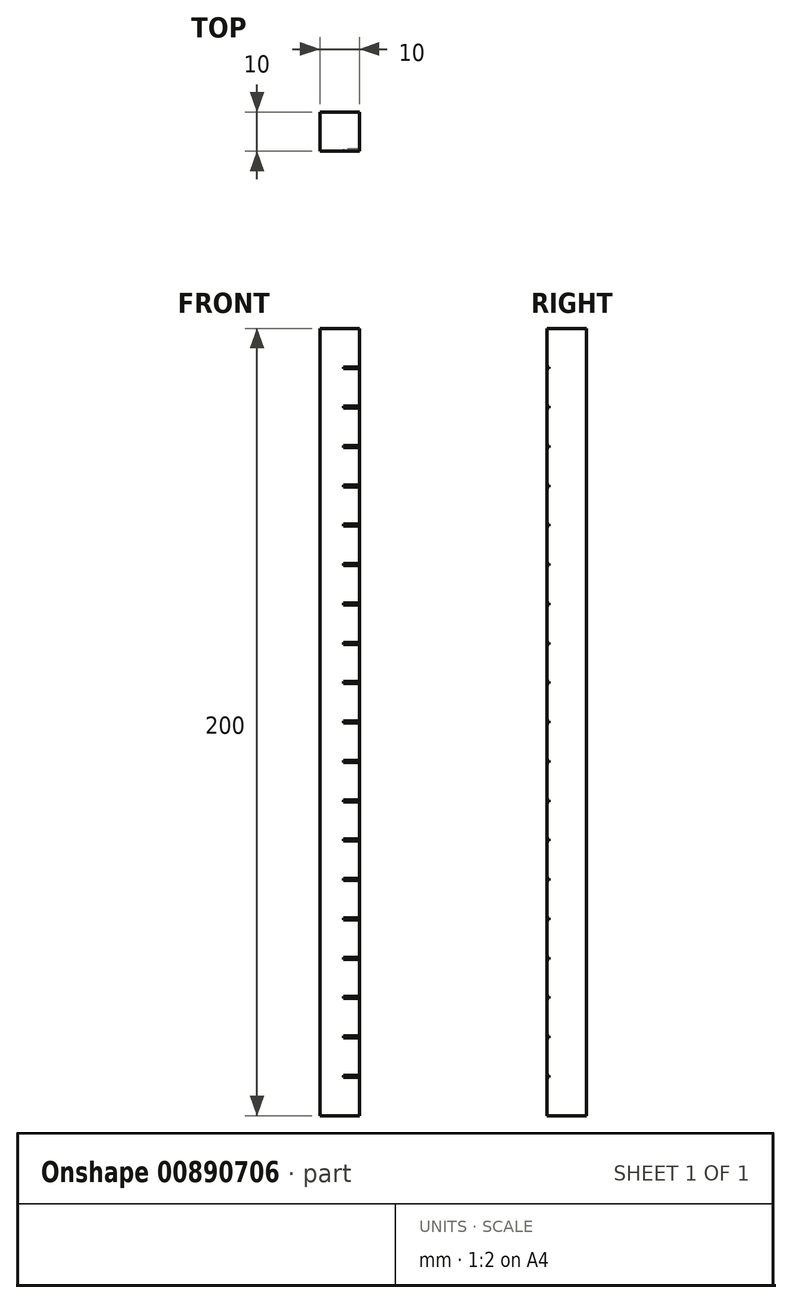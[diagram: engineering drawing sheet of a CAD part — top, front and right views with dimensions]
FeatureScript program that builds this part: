
annotation { "Feature Type Name" : "Feature", "Feature Type Description" : "" }
export const myFeature = defineFeature(function(context is Context, id is Id, definition is map)
    precondition{}
    {
        {
            var Q0;
            Q0=qCreatedBy(makeId("Top.planeOp"),FACE);
            var sketch = newSketch(context, id + "F0", { "sketchPlane" : qUnion([Q0])});
            skLineSegment(sketch, "E0.bottom", {"start": v(0, 0) * mm, "end": v(10, 0) * mm});
            skLineSegment(sketch, "E0.top", {"start": v(0, 10) * mm, "end": v(10, 10) * mm});
            skLineSegment(sketch, "E0.left", {"start": v(0, 0) * mm, "end": v(0, 10) * mm});
            skLineSegment(sketch, "E0.right", {"start": v(10, 0) * mm, "end": v(10, 10) * mm});
            skSolve(sketch);
        }
        {
            var Q0;
            Q0 = qSketchRegion(id + "F0", true);
            extrude(context, id + "F1", {"entities" : qUnion([Q0]), "depth" : 200 * mm, "offsetDistance" : 25 * mm});
        }
        {
            var Q0;
            Q0=makeQuery(id+"F1.opExtrude","SWEPT_FACE",FACE,{"disambiguationData":[OSD([sQuery(id+"F0.wireOp",EDGE,"E0.bottom")])]});
            var sketch = newSketch(context, id + "F2", { "sketchPlane" : qUnion([Q0])});
            skLineSegment(sketch, "E1", {"start": v(10, 0) * mm, "end": v(10, 10) * mm});
            skLineSegment(sketch, "E2.bottom", {"start": v(10, 9.75) * mm, "end": v(6, 9.75) * mm});
            skLineSegment(sketch, "E2.top", {"start": v(10, 10.25) * mm, "end": v(6, 10.25) * mm});
            skLineSegment(sketch, "E2.left", {"start": v(10, 9.75) * mm, "end": v(10, 10.25) * mm});
            skLineSegment(sketch, "E2.right", {"start": v(6, 9.75) * mm, "end": v(6, 10.25) * mm});
            skLineSegment(sketch, "E3.0.1.0", {"start": v(10, 20.25) * mm, "end": v(6, 20.25) * mm});
            skLineSegment(sketch, "E3.0.1.1", {"start": v(10, 19.75) * mm, "end": v(6, 19.75) * mm});
            skLineSegment(sketch, "E3.0.1.2", {"start": v(6, 19.75) * mm, "end": v(6, 20.25) * mm});
            skLineSegment(sketch, "E3.0.2.0", {"start": v(10, 30.25) * mm, "end": v(6, 30.25) * mm});
            skLineSegment(sketch, "E3.0.2.1", {"start": v(10, 29.75) * mm, "end": v(6, 29.75) * mm});
            skLineSegment(sketch, "E3.0.2.2", {"start": v(6, 29.75) * mm, "end": v(6, 30.25) * mm});
            skLineSegment(sketch, "E3.0.3.0", {"start": v(10, 40.25) * mm, "end": v(6, 40.25) * mm});
            skLineSegment(sketch, "E3.0.3.1", {"start": v(10, 39.75) * mm, "end": v(6, 39.75) * mm});
            skLineSegment(sketch, "E3.0.3.2", {"start": v(6, 39.75) * mm, "end": v(6, 40.25) * mm});
            skLineSegment(sketch, "E3.0.4.0", {"start": v(10, 50.25) * mm, "end": v(6, 50.25) * mm});
            skLineSegment(sketch, "E3.0.4.1", {"start": v(10, 49.75) * mm, "end": v(6, 49.75) * mm});
            skLineSegment(sketch, "E3.0.4.2", {"start": v(6, 49.75) * mm, "end": v(6, 50.25) * mm});
            skLineSegment(sketch, "E3.0.5.0", {"start": v(10, 60.25) * mm, "end": v(6, 60.25) * mm});
            skLineSegment(sketch, "E3.0.5.1", {"start": v(10, 59.75) * mm, "end": v(6, 59.75) * mm});
            skLineSegment(sketch, "E3.0.5.2", {"start": v(6, 59.75) * mm, "end": v(6, 60.25) * mm});
            skLineSegment(sketch, "E3.0.6.0", {"start": v(10, 70.25) * mm, "end": v(6, 70.25) * mm});
            skLineSegment(sketch, "E3.0.6.1", {"start": v(10, 69.75) * mm, "end": v(6, 69.75) * mm});
            skLineSegment(sketch, "E3.0.6.2", {"start": v(6, 69.75) * mm, "end": v(6, 70.25) * mm});
            skLineSegment(sketch, "E3.0.7.0", {"start": v(10, 80.25) * mm, "end": v(6, 80.25) * mm});
            skLineSegment(sketch, "E3.0.7.1", {"start": v(10, 79.75) * mm, "end": v(6, 79.75) * mm});
            skLineSegment(sketch, "E3.0.7.2", {"start": v(6, 79.75) * mm, "end": v(6, 80.25) * mm});
            skLineSegment(sketch, "E3.0.8.0", {"start": v(10, 90.25) * mm, "end": v(6, 90.25) * mm});
            skLineSegment(sketch, "E3.0.8.1", {"start": v(10, 89.75) * mm, "end": v(6, 89.75) * mm});
            skLineSegment(sketch, "E3.0.8.2", {"start": v(6, 89.75) * mm, "end": v(6, 90.25) * mm});
            skLineSegment(sketch, "E3.0.9.0", {"start": v(10, 100.25) * mm, "end": v(6, 100.25) * mm});
            skLineSegment(sketch, "E3.0.9.1", {"start": v(10, 99.75) * mm, "end": v(6, 99.75) * mm});
            skLineSegment(sketch, "E3.0.9.2", {"start": v(6, 99.75) * mm, "end": v(6, 100.25) * mm});
            skLineSegment(sketch, "E3.0.10.0", {"start": v(10, 110.25) * mm, "end": v(6, 110.25) * mm});
            skLineSegment(sketch, "E3.0.10.1", {"start": v(10, 109.75) * mm, "end": v(6, 109.75) * mm});
            skLineSegment(sketch, "E3.0.10.2", {"start": v(6, 109.75) * mm, "end": v(6, 110.25) * mm});
            skLineSegment(sketch, "E3.0.11.0", {"start": v(10, 120.25) * mm, "end": v(6, 120.25) * mm});
            skLineSegment(sketch, "E3.0.11.1", {"start": v(10, 119.75) * mm, "end": v(6, 119.75) * mm});
            skLineSegment(sketch, "E3.0.11.2", {"start": v(6, 119.75) * mm, "end": v(6, 120.25) * mm});
            skLineSegment(sketch, "E3.0.12.0", {"start": v(10, 130.25) * mm, "end": v(6, 130.25) * mm});
            skLineSegment(sketch, "E3.0.12.1", {"start": v(10, 129.75) * mm, "end": v(6, 129.75) * mm});
            skLineSegment(sketch, "E3.0.12.2", {"start": v(6, 129.75) * mm, "end": v(6, 130.25) * mm});
            skLineSegment(sketch, "E3.0.13.0", {"start": v(10, 140.25) * mm, "end": v(6, 140.25) * mm});
            skLineSegment(sketch, "E3.0.13.1", {"start": v(10, 139.75) * mm, "end": v(6, 139.75) * mm});
            skLineSegment(sketch, "E3.0.13.2", {"start": v(6, 139.75) * mm, "end": v(6, 140.25) * mm});
            skLineSegment(sketch, "E3.0.14.0", {"start": v(10, 150.25) * mm, "end": v(6, 150.25) * mm});
            skLineSegment(sketch, "E3.0.14.1", {"start": v(10, 149.75) * mm, "end": v(6, 149.75) * mm});
            skLineSegment(sketch, "E3.0.14.2", {"start": v(6, 149.75) * mm, "end": v(6, 150.25) * mm});
            skLineSegment(sketch, "E3.0.15.0", {"start": v(10, 160.25) * mm, "end": v(6, 160.25) * mm});
            skLineSegment(sketch, "E3.0.15.1", {"start": v(10, 159.75) * mm, "end": v(6, 159.75) * mm});
            skLineSegment(sketch, "E3.0.15.2", {"start": v(6, 159.75) * mm, "end": v(6, 160.25) * mm});
            skLineSegment(sketch, "E3.0.16.0", {"start": v(10, 170.25) * mm, "end": v(6, 170.25) * mm});
            skLineSegment(sketch, "E3.0.16.1", {"start": v(10, 169.75) * mm, "end": v(6, 169.75) * mm});
            skLineSegment(sketch, "E3.0.16.2", {"start": v(6, 169.75) * mm, "end": v(6, 170.25) * mm});
            skLineSegment(sketch, "E3.0.17.0", {"start": v(10, 180.25) * mm, "end": v(6, 180.25) * mm});
            skLineSegment(sketch, "E3.0.17.1", {"start": v(10, 179.75) * mm, "end": v(6, 179.75) * mm});
            skLineSegment(sketch, "E3.0.17.2", {"start": v(6, 179.75) * mm, "end": v(6, 180.25) * mm});
            skLineSegment(sketch, "E3.0.18.0", {"start": v(10, 190.25) * mm, "end": v(6, 190.25) * mm});
            skLineSegment(sketch, "E3.0.18.1", {"start": v(10, 189.75) * mm, "end": v(6, 189.75) * mm});
            skLineSegment(sketch, "E3.0.18.2", {"start": v(6, 189.75) * mm, "end": v(6, 190.25) * mm});
            skLineSegment(sketch, "E3.direction1", {"start": v(6, 10.25) * mm, "end": v(31, 10.25) * mm, "construction": true});
            skLineSegment(sketch, "E3.direction2", {"start": v(6, 10.25) * mm, "end": v(6, 20.25) * mm, "construction": true});
            skSolve(sketch);
        }
        {
            var Q0;
            Q0 = qSketchRegion(id + "F2", true);
            var Q1;
            {var subQ0=sQuery(id+"F2.wireOp",EDGE,"E3.0.1.0");Q1=makeQuery(id+"F2.imprint","IMPRINT",FACE,{"disambiguationData":[TD([[makeQuery(id+"F2.imprint","IMPRINT",EDGE,{"derivedFrom":subQ0}),1.0]])]});}
            var Q2;
            {var subQ0=sQuery(id+"F2.wireOp",EDGE,"E3.0.2.0");Q2=makeQuery(id+"F2.imprint","IMPRINT",FACE,{"disambiguationData":[TD([[makeQuery(id+"F2.imprint","IMPRINT",EDGE,{"derivedFrom":subQ0}),1.0]])]});}
            var Q3;
            {var subQ0=sQuery(id+"F2.wireOp",EDGE,"E3.0.3.0");Q3=makeQuery(id+"F2.imprint","IMPRINT",FACE,{"disambiguationData":[TD([[makeQuery(id+"F2.imprint","IMPRINT",EDGE,{"derivedFrom":subQ0}),1.0]])]});}
            var Q4;
            {var subQ0=sQuery(id+"F2.wireOp",EDGE,"E3.0.4.0");Q4=makeQuery(id+"F2.imprint","IMPRINT",FACE,{"disambiguationData":[TD([[makeQuery(id+"F2.imprint","IMPRINT",EDGE,{"derivedFrom":subQ0}),1.0]])]});}
            var Q5;
            {var subQ0=sQuery(id+"F2.wireOp",EDGE,"E3.0.5.0");Q5=makeQuery(id+"F2.imprint","IMPRINT",FACE,{"disambiguationData":[TD([[makeQuery(id+"F2.imprint","IMPRINT",EDGE,{"derivedFrom":subQ0}),1.0]])]});}
            var Q6;
            {var subQ0=sQuery(id+"F2.wireOp",EDGE,"E3.0.6.0");Q6=makeQuery(id+"F2.imprint","IMPRINT",FACE,{"disambiguationData":[TD([[makeQuery(id+"F2.imprint","IMPRINT",EDGE,{"derivedFrom":subQ0}),1.0]])]});}
            var Q7;
            {var subQ0=sQuery(id+"F2.wireOp",EDGE,"E3.0.7.0");Q7=makeQuery(id+"F2.imprint","IMPRINT",FACE,{"disambiguationData":[TD([[makeQuery(id+"F2.imprint","IMPRINT",EDGE,{"derivedFrom":subQ0}),1.0]])]});}
            var Q8;
            {var subQ0=sQuery(id+"F2.wireOp",EDGE,"E3.0.8.0");Q8=makeQuery(id+"F2.imprint","IMPRINT",FACE,{"disambiguationData":[TD([[makeQuery(id+"F2.imprint","IMPRINT",EDGE,{"derivedFrom":subQ0}),1.0]])]});}
            var Q9;
            {var subQ0=sQuery(id+"F2.wireOp",EDGE,"E3.0.9.0");Q9=makeQuery(id+"F2.imprint","IMPRINT",FACE,{"disambiguationData":[TD([[makeQuery(id+"F2.imprint","IMPRINT",EDGE,{"derivedFrom":subQ0}),1.0]])]});}
            var Q10;
            {var subQ0=sQuery(id+"F2.wireOp",EDGE,"E3.0.10.0");Q10=makeQuery(id+"F2.imprint","IMPRINT",FACE,{"disambiguationData":[TD([[makeQuery(id+"F2.imprint","IMPRINT",EDGE,{"derivedFrom":subQ0}),1.0]])]});}
            var Q11;
            {var subQ0=sQuery(id+"F2.wireOp",EDGE,"E3.0.11.0");Q11=makeQuery(id+"F2.imprint","IMPRINT",FACE,{"disambiguationData":[TD([[makeQuery(id+"F2.imprint","IMPRINT",EDGE,{"derivedFrom":subQ0}),1.0]])]});}
            var Q12;
            {var subQ0=sQuery(id+"F2.wireOp",EDGE,"E3.0.12.0");Q12=makeQuery(id+"F2.imprint","IMPRINT",FACE,{"disambiguationData":[TD([[makeQuery(id+"F2.imprint","IMPRINT",EDGE,{"derivedFrom":subQ0}),1.0]])]});}
            var Q13;
            {var subQ0=sQuery(id+"F2.wireOp",EDGE,"E3.0.13.0");Q13=makeQuery(id+"F2.imprint","IMPRINT",FACE,{"disambiguationData":[TD([[makeQuery(id+"F2.imprint","IMPRINT",EDGE,{"derivedFrom":subQ0}),1.0]])]});}
            var Q14;
            {var subQ0=sQuery(id+"F2.wireOp",EDGE,"E3.0.14.0");Q14=makeQuery(id+"F2.imprint","IMPRINT",FACE,{"disambiguationData":[TD([[makeQuery(id+"F2.imprint","IMPRINT",EDGE,{"derivedFrom":subQ0}),1.0]])]});}
            var Q15;
            {var subQ0=sQuery(id+"F2.wireOp",EDGE,"E3.0.15.0");Q15=makeQuery(id+"F2.imprint","IMPRINT",FACE,{"disambiguationData":[TD([[makeQuery(id+"F2.imprint","IMPRINT",EDGE,{"derivedFrom":subQ0}),1.0]])]});}
            var Q16;
            {var subQ0=sQuery(id+"F2.wireOp",EDGE,"E3.0.16.0");Q16=makeQuery(id+"F2.imprint","IMPRINT",FACE,{"disambiguationData":[TD([[makeQuery(id+"F2.imprint","IMPRINT",EDGE,{"derivedFrom":subQ0}),1.0]])]});}
            var Q17;
            {var subQ0=sQuery(id+"F2.wireOp",EDGE,"E3.0.17.0");Q17=makeQuery(id+"F2.imprint","IMPRINT",FACE,{"disambiguationData":[TD([[makeQuery(id+"F2.imprint","IMPRINT",EDGE,{"derivedFrom":subQ0}),1.0]])]});}
            var Q18;
            {var subQ0=sQuery(id+"F2.wireOp",EDGE,"E3.0.18.0");Q18=makeQuery(id+"F2.imprint","IMPRINT",FACE,{"disambiguationData":[TD([[makeQuery(id+"F2.imprint","IMPRINT",EDGE,{"derivedFrom":subQ0}),1.0]])]});}
            extrude(context, id + "F3", {"entities" : qUnion([Q0, Q1, Q2, Q3, Q4, Q5, Q6, Q7, Q8, Q9, Q10, Q11, Q12, Q13, Q14, Q15, Q16, Q17, Q18]), "operationType" : NewBodyOperationType.REMOVE, "oppositeDirection" : true, "depth" : 0.5 * mm, "offsetDistance" : 25 * mm});
        }
    });
